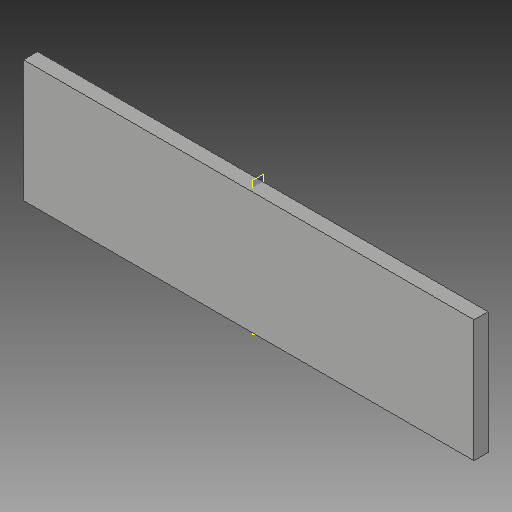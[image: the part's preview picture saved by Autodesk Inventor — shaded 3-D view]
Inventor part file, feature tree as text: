
AUTODESK INVENTOR PART (.ipt)
format: ipt  version: 2018 (Build 220112000, 112)  size: 126,976 bytes
history: native  units: mm
features: other x6, plane x1, sheet_metal_op x1, sketch x1, reference x1
ambient origin geometry x8: Origin, YZ Plane, XZ Plane, XY Plane, X Axis, Y Axis, Z Axis, Center Point
bodies: Solid1 (feature_tree)
feature tree (10):
  plane  "Work Plane1"
  sheet_metal_op  "Face1"
  other  "midtplan"
  sketch  "Sketch1"  dims[d7=3.0mm d8=12.0mm d9=12.0mm d10=26.0mm]
  reference  "Reference1"
  other  "Plate1"
  parser-record x1  (decoder bookkeeping rows leaked as tree rows — omitted from the tree; the rows remain in map.json)
  other  "modul.iam"
  other  "plade:1"
  other  "Definition1"
note: 1 file-system path scrubbed to <path> (originals preserved in map.json)
